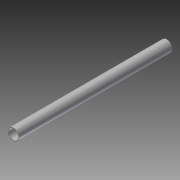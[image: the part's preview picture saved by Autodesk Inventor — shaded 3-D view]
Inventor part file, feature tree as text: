
AUTODESK INVENTOR PART (.ipt)
format: ipt  version: 2014 (Build 180170000, 170)  size: 72,704 bytes
history: native  units: in
note: dims shown in document units (in); Inventor stores cm internally (conversion verified against a paired STEP export)
features: extrude x1, sketch x1
ambient origin geometry x8: Origin, YZ Plane, XZ Plane, XY Plane, X Axis, Y Axis, Z Axis, Center Point
bodies: Solid1 (feature_tree)
feature tree (2):
  extrude  "Extrusion1"  Depth=6.75in TaperAngle=0.0deg
  sketch  "Sketch1"  dims[d0=0.5in d1=6.75in d2=0.0in d3=0.028in]
